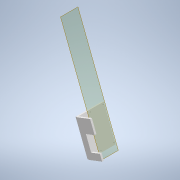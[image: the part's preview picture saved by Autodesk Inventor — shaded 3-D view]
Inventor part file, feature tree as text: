
AUTODESK INVENTOR PART (.ipt)
format: ipt  version: 2021 (Build 250183000, 183)  size: 192,512 bytes
history: native  units: mm
features: reference x11, extrude x6, sketch x6, other x3, plane x2, draft x1, fillet x1
ambient origin geometry x8: Origin, YZ Plane, XZ Plane, XY Plane, X Axis, Y Axis, Z Axis, Center Point
bodies: Solid1 (feature_tree)
feature tree (30):
  plane  "Work Plane1"
  extrude  "Extrusion1"  Depth=5.0mm
  extrude  "Extrusion2"  Depth=40.0mm TaperAngle=0.0deg
  sketch  "Sketch3"  dims[d6=40.0mm d7=0.0mm d8=0.436332mm]
  plane  "Work Plane2"
  extrude  "Extrusion3"  Depth=40.0mm
  draft  "FaceDraft1"
  extrude  "Extrusion4"  TaperAngle=0.0deg  [1 undecoded]
  extrude  "Extrusion5"  TaperAngle=0.0deg  [1 undecoded]
  extrude  "Extrusion6"  [1 undecoded]
  fillet  "Fillet1"  [1 undecoded]
  sketch  "Sketch1"  dims[d0=5.0mm d1=0.0mm d2=5.0mm]
  reference  "Reference1"
  reference  "Reference2"
  reference  "Reference3"
  sketch  "Sketch2"  dims[d3=180.0deg d4=40.0mm d5=0.0mm]
  reference  "Reference4"
  reference  "Reference5"
  reference  "Reference6"
  sketch  "Sketch4"  dims[d9=40.0mm d10=0.0mm d11=0.0mm d12=0.0mm]
  sketch  "Sketch5"  dims[d13=5.0mm d14=0.0mm d15=0.0mm]
  reference  "Reference7"
  reference  "Reference8"
  reference  "Reference9"
  reference  "Reference10"
  reference  "Reference11"
  sketch  "Sketch6"  dims[d16=5.0mm]
  other  "4_WheelsSwerve01.iam"
  other  "Part10"
  other  "Part13:1"
note: 4 required parameter values undecoded (feature->parameter linkage not recoverable at this tier; creation-order binding heuristic only, values carry confidence <= 0.55)
